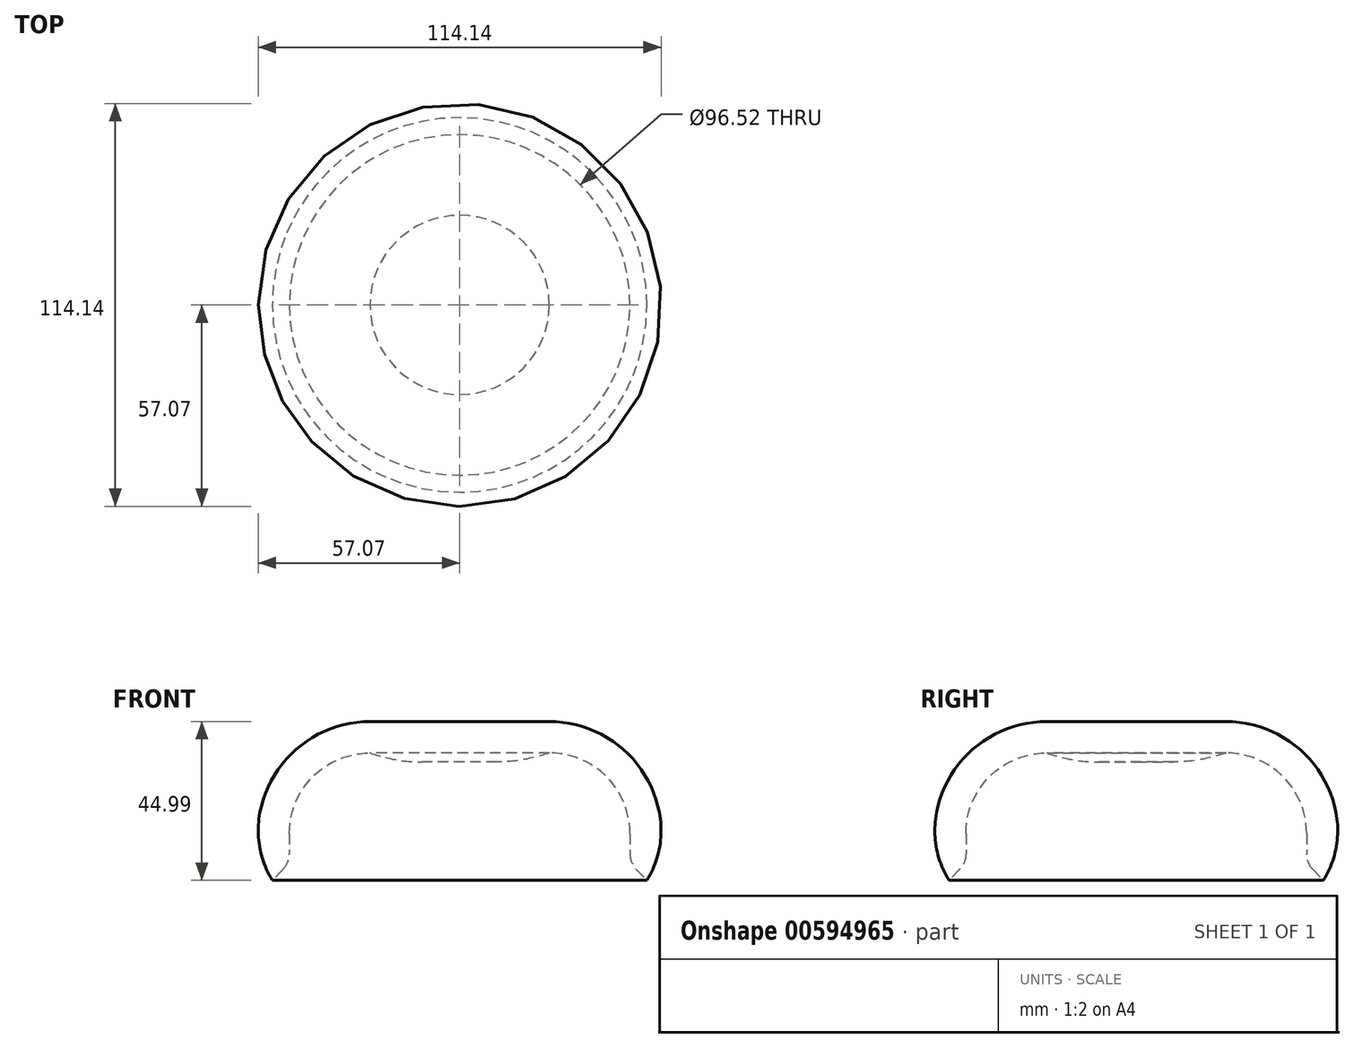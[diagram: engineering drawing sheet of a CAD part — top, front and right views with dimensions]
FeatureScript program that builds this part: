
annotation { "Feature Type Name" : "Feature", "Feature Type Description" : "" }
export const myFeature = defineFeature(function(context is Context, id is Id, definition is map)
    precondition{}
    {
        {
            var Q0;
            Q0=qCreatedBy(makeId("Top.planeOp"),FACE);
            var sketch = newSketch(context, id + "F0", { "sketchPlane" : qUnion([Q0])});
            skCircle(sketch, "E0", {"center": v(0, 0) * mm, "radius": 57.15 * mm});
            skSolve(sketch);
        }
        {
            var Q0;
            Q0 = qSketchRegion(id + "F0", true);
            extrude(context, id + "F1", {"entities" : qUnion([Q0]), "depth" : 50.8 * mm, "offsetDistance" : 25.4 * mm});
        }
        {
            var Q0;
            Q0=makeQuery(id+"F1.opExtrude","CAP_EDGE",EDGE,{"disambiguationData":[OSD([sQuery(id+"F0.wireOp",EDGE,"E0")])],"isStart":false});
            fillet(context, id + "F2", {"entities" : qUnion([Q0]), "radius" : 31.75 * mm, "tangentPropagation" : true, "allowEdgeOverflow" : false});
        }
        {
            var Q0;
            Q0=makeQuery(id+"F1.opExtrude","CAP_FACE",FACE,{"disambiguationData":[OSD([sQuery(id+"F0.wireOp",EDGE,"E0")])],"isStart":true});
            shell(context, id + "F3", {"entities" : qUnion([Q0]), "thickness" : 8.9 * mm});
        }
        {
            var Q0;
            Q0=makeQuery(id+"F1.opExtrude","CAP_EDGE",EDGE,{"disambiguationData":[OSD([sQuery(id+"F0.wireOp",EDGE,"E0")])],"isStart":true});
            fillet(context, id + "F4", {"entities" : qUnion([Q0]), "radius" : 26.98 * mm, "tangentPropagation" : true, "allowEdgeOverflow" : false});
        }
        {
            var Q0;
            {var subQ0=sQuery(id+"F0.wireOp",EDGE,"E0");Q0=makeQuery(id+"F4.opFillet","BLEND_EDGE",EDGE,{"blendedFrom":[makeQuery(id+"F1.opExtrude","CAP_EDGE",EDGE,{"disambiguationData":[OSD([subQ0])],"isStart":true}),makeQuery(id+"F3.opShell","OFFSET_FACE",FACE,{"disambiguationData":[OSD([subQ0]),TDD([makeQuery(id+"F1.opExtrude","SWEPT_FACE",FACE,{"disambiguationData":[OSD([subQ0])]})])]})],"blendedInto":[makeQuery(id+"F3.opShell","OFFSET_FACE",FACE,{"disambiguationData":[OSD([subQ0]),TDD([makeQuery(id+"F1.opExtrude","SWEPT_FACE",FACE,{"disambiguationData":[OSD([subQ0])]})])]})]});}
            chamfer(context, id + "F5", {"entities" : qUnion([Q0]), "chamferType" : ChamferType.OFFSET_ANGLE, "width" : 6.35 * mm, "oppositeDirection" : false, "angle" : 45 * degree, "tangentPropagation" : true});
        }
        {
            var Q0;
            {var subQ0=sQuery(id+"F0.wireOp",EDGE,"E0");var subQ1=makeQuery(id+"F3.opShell","OFFSET_FACE",FACE,{"disambiguationData":[OSD([subQ0]),TDD([makeQuery(id+"F1.opExtrude","SWEPT_FACE",FACE,{"disambiguationData":[OSD([subQ0])]})])]});Q0=makeQuery(id+"F5.opChamfer","BLEND_EDGE",EDGE,{"blendedFrom":[makeQuery(id+"F4.opFillet","BLEND_EDGE",EDGE,{"blendedFrom":[makeQuery(id+"F1.opExtrude","CAP_EDGE",EDGE,{"disambiguationData":[OSD([subQ0])],"isStart":true}),subQ1],"blendedInto":[subQ1]}),subQ1],"blendedInto":[subQ1]});}
            chamfer(context, id + "F6", {"entities" : qUnion([Q0]), "width" : 5.08 * mm, "tangentPropagation" : true});
        }
        {
            var Q0;
            {var subQ0=sQuery(id+"F0.wireOp",EDGE,"E0");var subQ1=makeQuery(id+"F3.opShell","OFFSET_FACE",FACE,{"disambiguationData":[OSD([subQ0]),TDD([makeQuery(id+"F1.opExtrude","SWEPT_FACE",FACE,{"disambiguationData":[OSD([subQ0])]})])]});Q0=makeQuery(id+"F6.opChamfer","BLEND_EDGE",EDGE,{"blendedFrom":[makeQuery(id+"F5.opChamfer","BLEND_EDGE",EDGE,{"blendedFrom":[makeQuery(id+"F4.opFillet","BLEND_EDGE",EDGE,{"blendedFrom":[makeQuery(id+"F1.opExtrude","CAP_EDGE",EDGE,{"disambiguationData":[OSD([subQ0])],"isStart":true}),subQ1],"blendedInto":[subQ1]}),subQ1],"blendedInto":[subQ1]}),subQ1],"blendedInto":[subQ1]});}
            fillet(context, id + "F7", {"entities" : qUnion([Q0]), "radius" : 6.35 * mm, "tangentPropagation" : true, "allowEdgeOverflow" : false});
        }
        {
            var Q0;
            {var subQ0=sQuery(id+"F0.wireOp",EDGE,"E0");Q0=makeQuery(id+"F3.opShell","OFFSET_FACE",FACE,{"disambiguationData":[OSD([subQ0]),TDD([makeQuery(id+"F1.opExtrude","CAP_FACE",FACE,{"disambiguationData":[OSD([subQ0])],"isStart":false})])]});}
            extrude(context, id + "F8", {"entities" : qUnion([Q0]), "operationType" : NewBodyOperationType.ADD, "depth" : 2.54 * mm, "offsetDistance" : 25.4 * mm});
        }
        {
            var Q0;
            Q0=makeQuery(id+"F8.opExtrude","CAP_EDGE",EDGE,{"disambiguationData":[OSD([sQuery(id+"F0.wireOp",EDGE,"E0")])],"isStart":false});
            fillet(context, id + "F9", {"entities" : qUnion([Q0]), "radius" : 44.45 * mm, "tangentPropagation" : true, "allowEdgeOverflow" : false});
        }
    });
